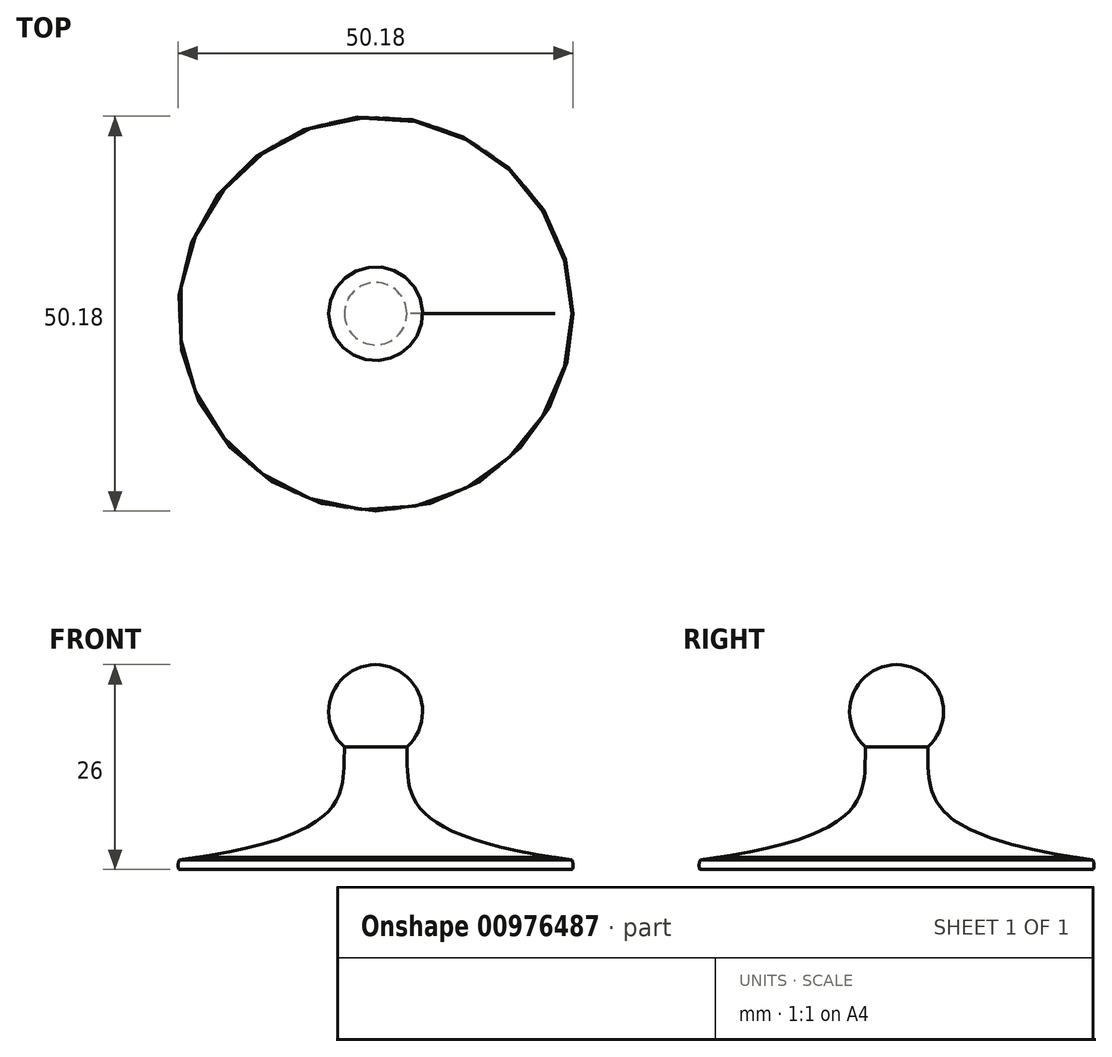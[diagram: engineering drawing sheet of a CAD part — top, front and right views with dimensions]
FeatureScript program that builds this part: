
annotation { "Feature Type Name" : "Feature", "Feature Type Description" : "" }
export const myFeature = defineFeature(function(context is Context, id is Id, definition is map)
    precondition{}
    {
        {
            var Q0;
            Q0=qCreatedBy(makeId("Front.planeOp"),FACE);
            var sketch = newSketch(context, id + "F0", { "sketchPlane" : qUnion([Q0])});
            skLineSegment(sketch, "E0", {"start": v(0, 0) * mm, "end": v(25, 0) * mm});
            skFitSpline(sketch, "E1", {"points": [v(24.92, 1.2) * mm, v(3.96, 15.53) * mm], "startDerivative": vector(-66.76, 9.1) * mm, "endDerivative": vector(-0.56, 18.32) * mm});
            skArc(sketch, "E2", {"start": v(3.96, 15.53) * mm, "mid": v(5.57, 22.12) * mm, "end": v(0, 26) * mm});
            skLineSegment(sketch, "E3", {"start": v(0, 34.51) * mm, "end": v(0, -21.01) * mm, "construction": true});
            skLineSegment(sketch, "E4", {"start": v(24.92, 1.2) * mm, "end": v(22.77, 1.5) * mm});
            skArc(sketch, "E5", {"start": v(25, 0) * mm, "mid": v(25.09, 0.6) * mm, "end": v(24.92, 1.2) * mm});
            skLineSegment(sketch, "E6", {"start": v(0, 26) * mm, "end": v(0, 0) * mm});
            skSolve(sketch);
        }
        {
            var Q0;
            Q0=makeQuery(id+"F0.imprint","IMPRINT",FACE,{"disambiguationData":[TD([[makeQuery(id+"F0.imprint","IMPRINT",EDGE,{"derivedFrom":sQuery(id+"F0.wireOp",EDGE,"E0")}),1.0]])]});
            var Q1;
            Q1=sQuery(id+"F0.wireOp",EDGE,"E6");
            revolve(context, id + "F1", {"surfaceOperationType" : NewSurfaceOperationType.NEW, "entities" : qUnion([Q0]), "axis" : qUnion([Q1]), "revolveType" : RevolveType.FULL});
        }
    });
